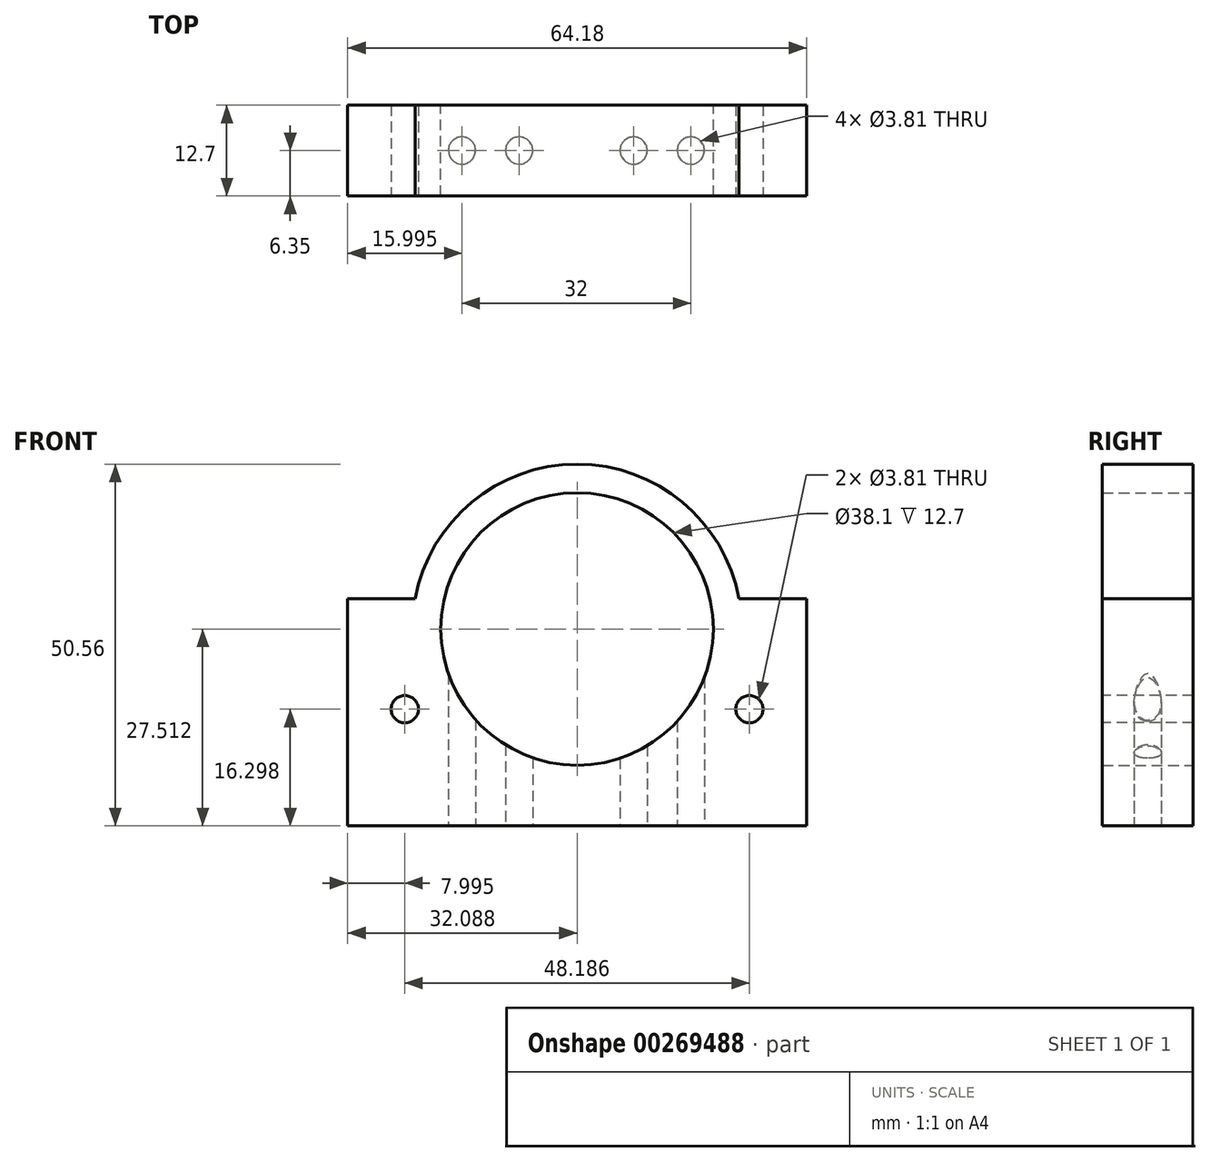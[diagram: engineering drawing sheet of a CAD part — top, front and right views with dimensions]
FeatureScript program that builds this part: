
annotation { "Feature Type Name" : "Feature", "Feature Type Description" : "" }
export const myFeature = defineFeature(function(context is Context, id is Id, definition is map)
    precondition{}
    {
        {
            var Q0;
            Q0=qCreatedBy(makeId("Front.planeOp"),FACE);
            var sketch = newSketch(context, id + "F0", { "sketchPlane" : qUnion([Q0])});
            skCircle(sketch, "E0", {"center": v(-75.51, 13.18) * mm, "radius": 19.05 * mm});
            skLineSegment(sketch, "E1.bottom", {"start": v(-107.6, 17.42) * mm, "end": v(-43.42, 17.42) * mm});
            skLineSegment(sketch, "E1.top", {"start": v(-107.6, -14.33) * mm, "end": v(-43.42, -14.33) * mm});
            skLineSegment(sketch, "E1.left", {"start": v(-107.6, 17.42) * mm, "end": v(-107.6, -14.33) * mm});
            skLineSegment(sketch, "E1.right", {"start": v(-43.42, 17.42) * mm, "end": v(-43.42, -14.33) * mm});
            skCircle(sketch, "E2", {"center": v(-75.51, 13.18) * mm, "radius": 23.05 * mm});
            skPoint(sketch, "E3", {"position": v(-75.51, 17.42) * mm});
            skSolve(sketch);
        }
        {
            var Q0;
            Q0=makeQuery(id+"F0.imprint","IMPRINT",FACE,{"disambiguationData":[TD([[makeQuery(id+"F0.imprint","IMPRINT",EDGE,{"derivedFrom":sQuery(id+"F0.wireOp",EDGE,"E1.top")}),1.0]])]});
            var Q1;
            {var subQ0=sQuery(id+"F0.wireOp",EDGE,"E1.bottom");var subQ1=sQuery(id+"F0.wireOp",EDGE,"E0");var subQ2=makeQuery(id+"F0.imprint","INTERSECT",VERTEX,{"disambiguationData":[OD(0.0)],"derivedFrom":[subQ1,subQ0]});Q1=makeQuery(id+"F0.imprint","IMPRINT",FACE,{"disambiguationData":[TD([[makeQuery(id+"F0.imprint","IMPRINT",EDGE,{"disambiguationData":[TD([[subQ2,-1.0]])],"derivedFrom":subQ1}),-1.0]])]});}
            var Q2;
            {var subQ0=sQuery(id+"F0.wireOp",EDGE,"E1.bottom");var subQ1=sQuery(id+"F0.wireOp",EDGE,"E0");var subQ2=makeQuery(id+"F0.imprint","INTERSECT",VERTEX,{"disambiguationData":[OD(0.0)],"derivedFrom":[subQ1,subQ0]});Q2=makeQuery(id+"F0.imprint","IMPRINT",FACE,{"disambiguationData":[TD([[makeQuery(id+"F0.imprint","IMPRINT",EDGE,{"disambiguationData":[TD([[subQ2,1.0]])],"derivedFrom":subQ1}),-1.0]])]});}
            extrude(context, id + "F1", {"entities" : qUnion([Q0, Q1, Q2]), "depth" : 12.7 * mm});
        }
        {
            var Q0;
            Q0=makeQuery(id+"F1.opExtrude","CAP_FACE",FACE,{"disambiguationData":[OSD([sQuery(id+"F0.wireOp",EDGE,"E0"),sQuery(id+"F0.wireOp",EDGE,"E1.bottom"),sQuery(id+"F0.wireOp",EDGE,"E1.top"),sQuery(id+"F0.wireOp",EDGE,"E1.left"),sQuery(id+"F0.wireOp",EDGE,"E1.right"),sQuery(id+"F0.wireOp",EDGE,"E2")])],"isStart":false});
            var sketch = newSketch(context, id + "F2", { "sketchPlane" : qUnion([Q0])});
            skCircle(sketch, "E4", {"center": v(-99.6, 1.97) * mm, "radius": 1.9 * mm});
            skCircle(sketch, "E5", {"center": v(-51.42, 1.97) * mm, "radius": 1.9 * mm});
            skLineSegment(sketch, "E6", {"start": v(-99.6, 1.97) * mm, "end": v(-51.42, 1.97) * mm});
            skSolve(sketch);
        }
        {
            var Q0;
            Q0=makeQuery(id+"F2.imprint","IMPRINT",FACE,{"disambiguationData":[TD([[makeQuery(id+"F2.imprint","IMPRINT",EDGE,{"derivedFrom":sQuery(id+"F2.wireOp",EDGE,"E4")}),1.0]])]});
            var Q1;
            Q1=makeQuery(id+"F2.imprint","IMPRINT",FACE,{"disambiguationData":[TD([[makeQuery(id+"F2.imprint","IMPRINT",EDGE,{"derivedFrom":sQuery(id+"F2.wireOp",EDGE,"E5")}),1.0]])]});
            extrude(context, id + "F3", {"entities" : qUnion([Q0, Q1]), "operationType" : NewBodyOperationType.REMOVE, "oppositeDirection" : true, "depth" : 12.7 * mm});
        }
        {
            var Q0;
            Q0=makeQuery(id+"F1.opExtrude","SWEPT_FACE",FACE,{"disambiguationData":[OSD([sQuery(id+"F0.wireOp",EDGE,"E1.top")])]});
            var sketch = newSketch(context, id + "F4", { "sketchPlane" : qUnion([Q0])});
            skCircle(sketch, "E7", {"center": v(-91.6, 6.35) * mm, "radius": 1.9 * mm});
            skCircle(sketch, "E8", {"center": v(-83.6, 6.35) * mm, "radius": 1.9 * mm});
            skCircle(sketch, "E9", {"center": v(-67.6, 6.35) * mm, "radius": 1.9 * mm});
            skCircle(sketch, "E10", {"center": v(-59.6, 6.35) * mm, "radius": 1.9 * mm});
            skSolve(sketch);
        }
        {
            var Q0;
            Q0=makeQuery(id+"F4.imprint","IMPRINT",FACE,{"disambiguationData":[TD([[makeQuery(id+"F4.imprint","IMPRINT",EDGE,{"derivedFrom":sQuery(id+"F4.wireOp",EDGE,"E7")}),1.0]])]});
            var Q1;
            Q1=makeQuery(id+"F4.imprint","IMPRINT",FACE,{"disambiguationData":[TD([[makeQuery(id+"F4.imprint","IMPRINT",EDGE,{"derivedFrom":sQuery(id+"F4.wireOp",EDGE,"E8")}),1.0]])]});
            var Q2;
            Q2=makeQuery(id+"F4.imprint","IMPRINT",FACE,{"disambiguationData":[TD([[makeQuery(id+"F4.imprint","IMPRINT",EDGE,{"derivedFrom":sQuery(id+"F4.wireOp",EDGE,"E9")}),1.0]])]});
            var Q3;
            Q3=makeQuery(id+"F4.imprint","IMPRINT",FACE,{"disambiguationData":[TD([[makeQuery(id+"F4.imprint","IMPRINT",EDGE,{"derivedFrom":sQuery(id+"F4.wireOp",EDGE,"E10")}),1.0]])]});
            extrude(context, id + "F5", {"entities" : qUnion([Q0, Q1, Q2, Q3]), "operationType" : NewBodyOperationType.REMOVE, "oppositeDirection" : true, "depth" : 25.4 * mm});
        }
    });
